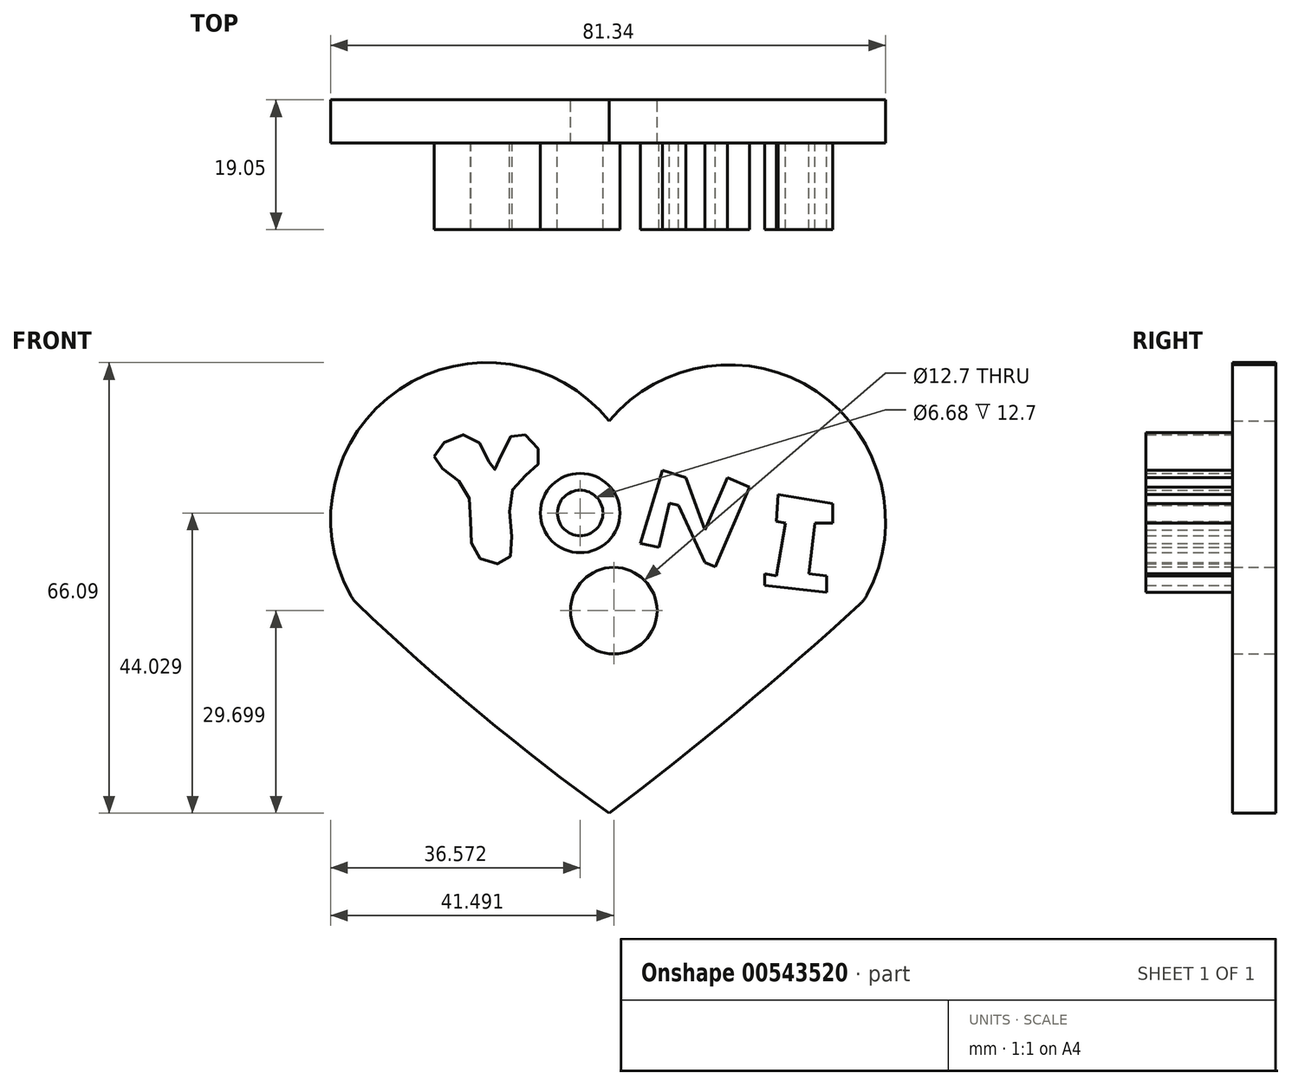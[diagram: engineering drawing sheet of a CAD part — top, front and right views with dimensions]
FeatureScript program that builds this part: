
annotation { "Feature Type Name" : "Feature", "Feature Type Description" : "" }
export const myFeature = defineFeature(function(context is Context, id is Id, definition is map)
    precondition{}
    {
        {
            var Q0;
            Q0=qCreatedBy(makeId("Front.planeOp"),FACE);
            var sketch = newSketch(context, id + "F0", { "sketchPlane" : qUnion([Q0])});
            skArc(sketch, "E0", {"start": v(-29.32, 44.92) * mm, "mid": v(-60.37, 49.34) * mm, "end": v(-66.75, 18.62) * mm});
            skArc(sketch, "E1", {"start": v(8.05, 18.62) * mm, "mid": v(1.5, 49) * mm, "end": v(-29.32, 44.92) * mm});
            skArc(sketch, "E2", {"start": v(-66.75, 18.62) * mm, "mid": v(-48.6, 2.35) * mm, "end": v(-29.32, -12.6) * mm});
            skArc(sketch, "E3", {"start": v(-29.32, -12.6) * mm, "mid": v(-10.25, 2.56) * mm, "end": v(8.05, 18.62) * mm});
            skSolve(sketch);
        }
        {
            var Q0;
            Q0=makeQuery(id+"F0.imprint","IMPRINT",FACE,{"disambiguationData":[TD([[makeQuery(id+"F0.imprint","IMPRINT",EDGE,{"derivedFrom":sQuery(id+"F0.wireOp",EDGE,"E0")}),1.0]])]});
            extrude(context, id + "F1", {"entities" : qUnion([Q0]), "depth" : 6.35 * mm, "offsetDistance" : 25.4 * mm});
        }
        {
            var Q0;
            Q0=makeQuery(id+"F1.opExtrude","SWEPT_EDGE",EDGE,{"disambiguationData":[OSD([sQuery(id+"F0.wireOp",EDGE,"E0"),sQuery(id+"F0.wireOp",EDGE,"E2")])]});
            fillet(context, id + "F2", {"entities" : qUnion([Q0]), "radius" : 5.08 * mm, "tangentPropagation" : true, "allowEdgeOverflow" : false});
        }
        {
            var Q0;
            Q0=makeQuery(id+"F1.opExtrude","SWEPT_EDGE",EDGE,{"disambiguationData":[OSD([sQuery(id+"F0.wireOp",EDGE,"E1"),sQuery(id+"F0.wireOp",EDGE,"E3")])]});
            fillet(context, id + "F3", {"entities" : qUnion([Q0]), "radius" : 5.08 * mm, "tangentPropagation" : true, "allowEdgeOverflow" : false});
        }
        {
            var Q0;
            Q0=makeQuery(id+"F1.opExtrude","CAP_FACE",FACE,{"disambiguationData":[OSD([sQuery(id+"F0.wireOp",EDGE,"E0"),sQuery(id+"F0.wireOp",EDGE,"E1"),sQuery(id+"F0.wireOp",EDGE,"E2"),sQuery(id+"F0.wireOp",EDGE,"E3")])],"isStart":true});
            var sketch = newSketch(context, id + "F4", { "sketchPlane" : qUnion([Q0])});
            skCircle(sketch, "E4", {"center": v(28.63, 17.1) * mm, "radius": 13.07 * mm});
            skSolve(sketch);
        }
        {
            var Q0;
            Q0=sQuery(id+"F4.wireOp",VERTEX,"E4.center");
            var Q1;
            Q1=makeQuery(id+"F1.opExtrude","SWEPT_BODY",BODY,{"disambiguationData":[OSD([sQuery(id+"F0.wireOp",EDGE,"E0"),sQuery(id+"F0.wireOp",EDGE,"E1"),sQuery(id+"F0.wireOp",EDGE,"E2"),sQuery(id+"F0.wireOp",EDGE,"E3")])]});
            hole(context, id + "F5", {"style" : HoleStyle.SIMPLE, "endStyle" : HoleEndStyle.THROUGH, "holeDiameter" : 12.7 * mm, "isTappedThrough" : true, "tappedDepth" : 12.7 * mm, "tapClearance" : 3, "locations" : qUnion([Q0]), "scope" : qUnion([Q1])});
        }
        {
            var Q0;
            Q0=makeQuery(id+"F1.opExtrude","CAP_FACE",FACE,{"disambiguationData":[OSD([sQuery(id+"F0.wireOp",EDGE,"E0"),sQuery(id+"F0.wireOp",EDGE,"E1"),sQuery(id+"F0.wireOp",EDGE,"E2"),sQuery(id+"F0.wireOp",EDGE,"E3")])],"isStart":false});
            var sketch = newSketch(context, id + "F6", { "sketchPlane" : qUnion([Q0])});
            skFitSpline(sketch, "E5", {"points": [v(-54.93, 39.73) * mm, v(-50.24, 34.8) * mm, v(-48.92, 25.46) * mm, v(-44.01, 24.74) * mm, v(-43.55, 34.7) * mm, v(-39.4, 39.44) * mm, v(-43.1, 43.1) * mm, v(-46.15, 37.76) * mm, v(-49.4, 42.7) * mm, v(-54.93, 39.73) * mm]});
            skCircle(sketch, "E6", {"center": v(-33.55, 31.44) * mm, "radius": 5.82 * mm});
            skLineSegment(sketch, "E7", {"start": v(-24.7, 27) * mm, "end": v(-21.48, 37.68) * mm});
            skLineSegment(sketch, "E8", {"start": v(-21.48, 37.68) * mm, "end": v(-18.04, 36.64) * mm});
            skLineSegment(sketch, "E9", {"start": v(-18.04, 36.64) * mm, "end": v(-15.27, 28.96) * mm});
            skLineSegment(sketch, "E10", {"start": v(-15.27, 28.96) * mm, "end": v(-11.97, 36.64) * mm});
            skLineSegment(sketch, "E11", {"start": v(-11.97, 36.64) * mm, "end": v(-8.73, 35.25) * mm});
            skLineSegment(sketch, "E12", {"start": v(-8.73, 35.25) * mm, "end": v(-13.76, 23.57) * mm});
            skLineSegment(sketch, "E13", {"start": v(-13.76, 23.57) * mm, "end": v(-15.27, 24.22) * mm});
            skLineSegment(sketch, "E14", {"start": v(-20.5, 32.87) * mm, "end": v(-22.01, 26.4) * mm});
            skLineSegment(sketch, "E15", {"start": v(-22.01, 26.4) * mm, "end": v(-24.7, 27) * mm});
            skLineSegment(sketch, "E16", {"start": v(-20.5, 32.87) * mm, "end": v(-19.15, 32.55) * mm});
            skLineSegment(sketch, "E17", {"start": v(-19.15, 32.55) * mm, "end": v(-15.27, 24.22) * mm});
            skLineSegment(sketch, "E18", {"start": v(-4.52, 34.12) * mm, "end": v(3.46, 32.84) * mm});
            skLineSegment(sketch, "E19", {"start": v(3.46, 32.84) * mm, "end": v(3.46, 29.97) * mm});
            skLineSegment(sketch, "E20", {"start": v(3.46, 29.97) * mm, "end": v(0.88, 29.97) * mm});
            skLineSegment(sketch, "E21", {"start": v(0.88, 29.97) * mm, "end": v(0, 22.5) * mm});
            skLineSegment(sketch, "E22", {"start": v(0, 22.5) * mm, "end": v(2.55, 22.2) * mm});
            skLineSegment(sketch, "E23", {"start": v(2.55, 22.2) * mm, "end": v(2.55, 19.77) * mm});
            skLineSegment(sketch, "E24", {"start": v(2.55, 19.77) * mm, "end": v(-6.51, 20.85) * mm});
            skLineSegment(sketch, "E25", {"start": v(-6.51, 20.85) * mm, "end": v(-6.51, 22.5) * mm});
            skLineSegment(sketch, "E26", {"start": v(-6.51, 22.5) * mm, "end": v(-4.8, 22.2) * mm});
            skLineSegment(sketch, "E27", {"start": v(-4.8, 22.2) * mm, "end": v(-3.43, 29.97) * mm});
            skLineSegment(sketch, "E28", {"start": v(-3.43, 29.97) * mm, "end": v(-4.8, 30.21) * mm});
            skLineSegment(sketch, "E29", {"start": v(-4.8, 30.21) * mm, "end": v(-4.52, 34.12) * mm});
            skCircle(sketch, "E30", {"center": v(-33.55, 31.44) * mm, "radius": 3.34 * mm});
            skSolve(sketch);
        }
        {
            var Q0;
            Q0=makeQuery(id+"F6.imprint","IMPRINT",FACE,{"disambiguationData":[TD([[makeQuery(id+"F6.imprint","IMPRINT",EDGE,{"derivedFrom":sQuery(id+"F6.wireOp",EDGE,"E5")}),1.0]])]});
            var Q1;
            Q1=makeQuery(id+"F6.imprint","IMPRINT",FACE,{"disambiguationData":[TD([[makeQuery(id+"F6.imprint","IMPRINT",EDGE,{"derivedFrom":sQuery(id+"F6.wireOp",EDGE,"E6")}),1.0]])]});
            var Q2;
            Q2=makeQuery(id+"F6.imprint","IMPRINT",FACE,{"disambiguationData":[TD([[makeQuery(id+"F6.imprint","IMPRINT",EDGE,{"derivedFrom":sQuery(id+"F6.wireOp",EDGE,"E7")}),-1.0]])]});
            var Q3;
            Q3=makeQuery(id+"F6.imprint","IMPRINT",FACE,{"disambiguationData":[TD([[makeQuery(id+"F6.imprint","IMPRINT",EDGE,{"derivedFrom":sQuery(id+"F6.wireOp",EDGE,"E18")}),-1.0]])]});
            extrude(context, id + "F7", {"entities" : qUnion([Q0, Q1, Q2, Q3]), "operationType" : NewBodyOperationType.ADD, "depth" : 12.7 * mm, "offsetDistance" : 25.4 * mm});
        }
    });
